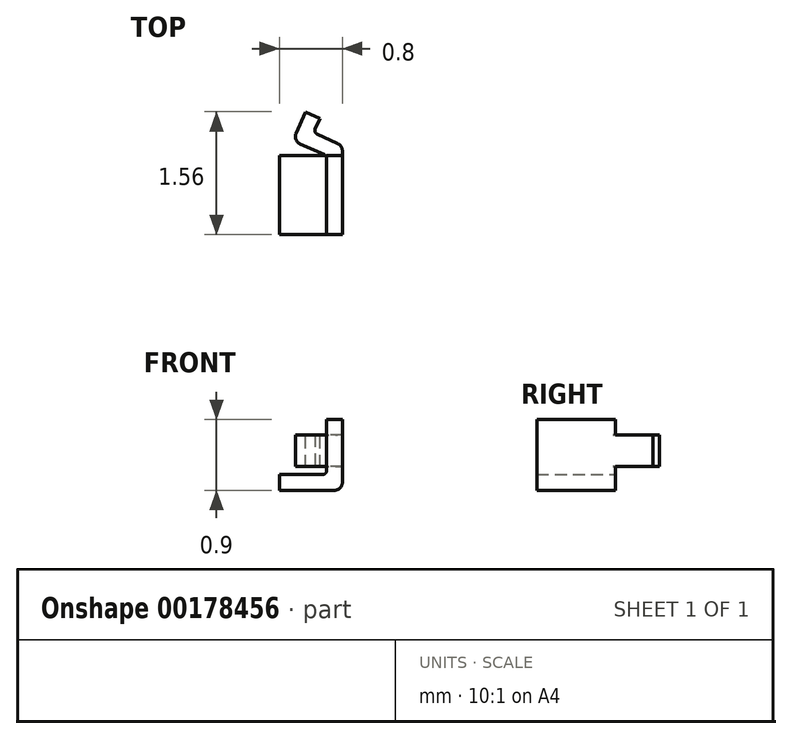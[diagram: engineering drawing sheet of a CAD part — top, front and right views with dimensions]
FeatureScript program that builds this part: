
annotation { "Feature Type Name" : "Feature", "Feature Type Description" : "" }
export const myFeature = defineFeature(function(context is Context, id is Id, definition is map)
    precondition{}
    {
        {
            var Q0;
            Q0=qCreatedBy(makeId("Front.planeOp"),FACE);
            var sketch = newSketch(context, id + "F0", { "sketchPlane" : qUnion([Q0])});
            skLineSegment(sketch, "E0.bottom", {"start": v(-0.4, 0.1) * mm, "end": v(0.4, 0.1) * mm});
            skLineSegment(sketch, "E0.top", {"start": v(-0.4, -0.1) * mm, "end": v(0.4, -0.1) * mm});
            skLineSegment(sketch, "E0.left", {"start": v(-0.4, 0.1) * mm, "end": v(-0.4, -0.1) * mm});
            skLineSegment(sketch, "E0.right", {"start": v(0.4, 0.1) * mm, "end": v(0.4, -0.1) * mm});
            skPoint(sketch, "E0.middle", {"position": v(0, 0) * mm});
            skLineSegment(sketch, "E1.bottom", {"start": v(0.4, 0.1) * mm, "end": v(0.2, 0.1) * mm});
            skLineSegment(sketch, "E1.top", {"start": v(0.4, 0.8) * mm, "end": v(0.2, 0.8) * mm});
            skLineSegment(sketch, "E1.left", {"start": v(0.4, 0.1) * mm, "end": v(0.4, 0.8) * mm});
            skLineSegment(sketch, "E1.right", {"start": v(0.2, 0.1) * mm, "end": v(0.2, 0.8) * mm});
            skSolve(sketch);
        }
        {
            var Q0;
            Q0 = qSketchRegion(id + "F0", true);
            extrude(context, id + "F1", {"entities" : qUnion([Q0]), "depth" : 1 * mm});
        }
        {
            var Q0;
            Q0=makeQuery(id+"F1.opExtrude","SWEPT_FACE",FACE,{"disambiguationData":[OSD([sQuery(id+"F0.wireOp",EDGE,"E1.top")])]});
            var sketch = newSketch(context, id + "F2", { "sketchPlane" : qUnion([Q0])});
            skLineSegment(sketch, "E2", {"start": v(0.2, 0) * mm, "end": v(-0.23, 0.2) * mm});
            skLineSegment(sketch, "E3", {"start": v(0.4, -0.07) * mm, "end": v(0.4, 0.13) * mm});
            skLineSegment(sketch, "E4", {"start": v(-0.15, 0.37) * mm, "end": v(0.4, 0.13) * mm});
            skLineSegment(sketch, "E5", {"start": v(-0.23, 0.2) * mm, "end": v(-0.15, 0.37) * mm});
            skLineSegment(sketch, "E6", {"start": v(-0.15, 0.37) * mm, "end": v(-0.07, 0.56) * mm});
            skLineSegment(sketch, "E7", {"start": v(-0.07, 0.56) * mm, "end": v(0.12, 0.48) * mm});
            skLineSegment(sketch, "E8", {"start": v(0.12, 0.48) * mm, "end": v(0.03, 0.3) * mm});
            skSolve(sketch);
        }
        {
            var Q0;
            Q0 = qSketchRegion(id + "F2", true);
            var Q1;
            Q1=makeQuery(id+"F2.imprint","IMPRINT",FACE,{"disambiguationData":[TD([[makeQuery(id+"F2.imprint","IMPRINT",EDGE,{"derivedFrom":sQuery(id+"F2.wireOp",EDGE,"E2")}),-1.0]])]});
            extrude(context, id + "F3", {"entities" : qUnion([Q0, Q1]), "operationType" : NewBodyOperationType.ADD, "oppositeDirection" : true, "depth" : 0.9 * mm});
        }
        {
            var Q0;
            {var subQ0=sQuery(id+"F0.wireOp",EDGE,"E1.top");Q0=makeQuery(id+"F3.boolean.opBoolean","MERGE",FACE,{"derivedFrom":[makeQuery(id+"F1.opExtrude","SWEPT_FACE",FACE,{"disambiguationData":[OSD([subQ0])]}),makeQuery(id+"F3.opExtrude","CAP_FACE",FACE,{"disambiguationData":[OSD([subQ0,sQuery(id+"F2.wireOp",EDGE,"E2"),sQuery(id+"F2.wireOp",EDGE,"E3"),sQuery(id+"F2.wireOp",EDGE,"E4"),sQuery(id+"F2.wireOp",EDGE,"E5"),sQuery(id+"F2.wireOp",EDGE,"E6"),sQuery(id+"F2.wireOp",EDGE,"E7"),sQuery(id+"F2.wireOp",EDGE,"E8")])],"isStart":true})]});}
            var sketch = newSketch(context, id + "F4", { "sketchPlane" : qUnion([Q0])});
            skLineSegment(sketch, "E9", {"start": v(0.4, 0) * mm, "end": v(0.2, 0) * mm});
            skSolve(sketch);
        }
        {
            var Q0;
            {var subQ1=sQuery(id+"F4.wireOp",EDGE,"E9");Q0=makeQuery(id+"F4.imprint","IMPRINT",FACE,{"disambiguationData":[TD([[makeQuery(id+"F4.imprint","IMPRINT",EDGE,{"derivedFrom":subQ1}),-1.0]])]});}
            extrude(context, id + "F5", {"entities" : qUnion([Q0]), "operationType" : NewBodyOperationType.REMOVE, "oppositeDirection" : true, "depth" : 0.2 * mm});
        }
        {
            var Q0;
            Q0=makeQuery(id+"F3.boolean.opBoolean","MERGE",FACE,{"derivedFrom":[makeQuery(id+"F1.opExtrude","SWEPT_FACE",FACE,{"disambiguationData":[OSD([sQuery(id+"F0.wireOp",EDGE,"E0.top")])]}),makeQuery(id+"F3.opExtrude","CAP_FACE",FACE,{"disambiguationData":[OSD([sQuery(id+"F0.wireOp",EDGE,"E1.top"),sQuery(id+"F2.wireOp",EDGE,"E2"),sQuery(id+"F2.wireOp",EDGE,"E3"),sQuery(id+"F2.wireOp",EDGE,"E4"),sQuery(id+"F2.wireOp",EDGE,"E5"),sQuery(id+"F2.wireOp",EDGE,"E6"),sQuery(id+"F2.wireOp",EDGE,"E7"),sQuery(id+"F2.wireOp",EDGE,"E8")])],"isStart":false})]});
            var sketch = newSketch(context, id + "F6", { "sketchPlane" : qUnion([Q0])});
            skLineSegment(sketch, "E10", {"start": v(0.4, 0) * mm, "end": v(0.2, 0) * mm});
            skSolve(sketch);
        }
        {
            var Q0;
            {var subQ0=sQuery(id+"F6.wireOp",EDGE,"E10");Q0=makeQuery(id+"F6.imprint","IMPRINT",FACE,{"disambiguationData":[TD([[makeQuery(id+"F6.imprint","IMPRINT",EDGE,{"derivedFrom":subQ0}),1.0]])]});}
            extrude(context, id + "F7", {"entities" : qUnion([Q0]), "operationType" : NewBodyOperationType.REMOVE, "oppositeDirection" : true, "depth" : 0.3 * mm});
        }
        {
            var Q0;
            Q0=makeQuery(id+"F3.opExtrude","SWEPT_EDGE",EDGE,{"disambiguationData":[OSD([sQuery(id+"F2.wireOp",EDGE,"E4"),sQuery(id+"F2.wireOp",EDGE,"E8")])]});
            var Q1;
            {var subQ0=sQuery(id+"F0.wireOp",EDGE,"E1.right");Q1=makeQuery(id+"F7.boolean.opBoolean","SPLIT",EDGE,{"derivedFrom":makeQuery(id+"F5.boolean.opBoolean","SPLIT",EDGE,{"derivedFrom":makeQuery(id+"F3.boolean.opBoolean","MERGE",EDGE,{"derivedFrom":[makeQuery(id+"F1.opExtrude","CAP_EDGE",EDGE,{"disambiguationData":[OSD([subQ0])],"isStart":true}),makeQuery(id+"F3.opExtrude","SWEPT_EDGE",EDGE,{"disambiguationData":[OSD([sQuery(id+"F0.wireOp",EDGE,"E1.top"),subQ0,sQuery(id+"F2.wireOp",EDGE,"E2")])]})]})})});}
            var Q2;
            Q2=makeQuery(id+"F1.opExtrude","SWEPT_EDGE",EDGE,{"disambiguationData":[OSD([sQuery(id+"F0.wireOp",EDGE,"E0.bottom"),sQuery(id+"F0.wireOp",EDGE,"E1.bottom"),sQuery(id+"F0.wireOp",EDGE,"E1.right")])]});
            fillet(context, id + "F8", {"entities" : qUnion([Q0, Q1, Q2]), "radius" : 0.05 * mm, "tangentPropagation" : true, "allowEdgeOverflow" : false});
        }
        {
            var Q0;
            Q0=makeQuery(id+"F3.boolean.opBoolean","MERGE",EDGE,{"derivedFrom":[makeQuery(id+"F1.opExtrude","SWEPT_EDGE",EDGE,{"disambiguationData":[OSD([sQuery(id+"F0.wireOp",EDGE,"E0.top"),sQuery(id+"F0.wireOp",EDGE,"E0.right")])]}),makeQuery(id+"F3.opExtrude","CAP_EDGE",EDGE,{"disambiguationData":[OSD([sQuery(id+"F2.wireOp",EDGE,"E3")])],"isStart":false})]});
            var Q1;
            Q1=makeQuery(id+"F3.opExtrude","SWEPT_EDGE",EDGE,{"disambiguationData":[OSD([sQuery(id+"F2.wireOp",EDGE,"E2"),sQuery(id+"F2.wireOp",EDGE,"E5")])]});
            var Q2;
            Q2=makeQuery(id+"F3.opExtrude","SWEPT_EDGE",EDGE,{"disambiguationData":[OSD([sQuery(id+"F2.wireOp",EDGE,"E3"),sQuery(id+"F2.wireOp",EDGE,"E4")])]});
            fillet(context, id + "F9", {"entities" : qUnion([Q0, Q1, Q2]), "radius" : 0.1 * mm, "tangentPropagation" : true, "allowEdgeOverflow" : false});
        }
    });
